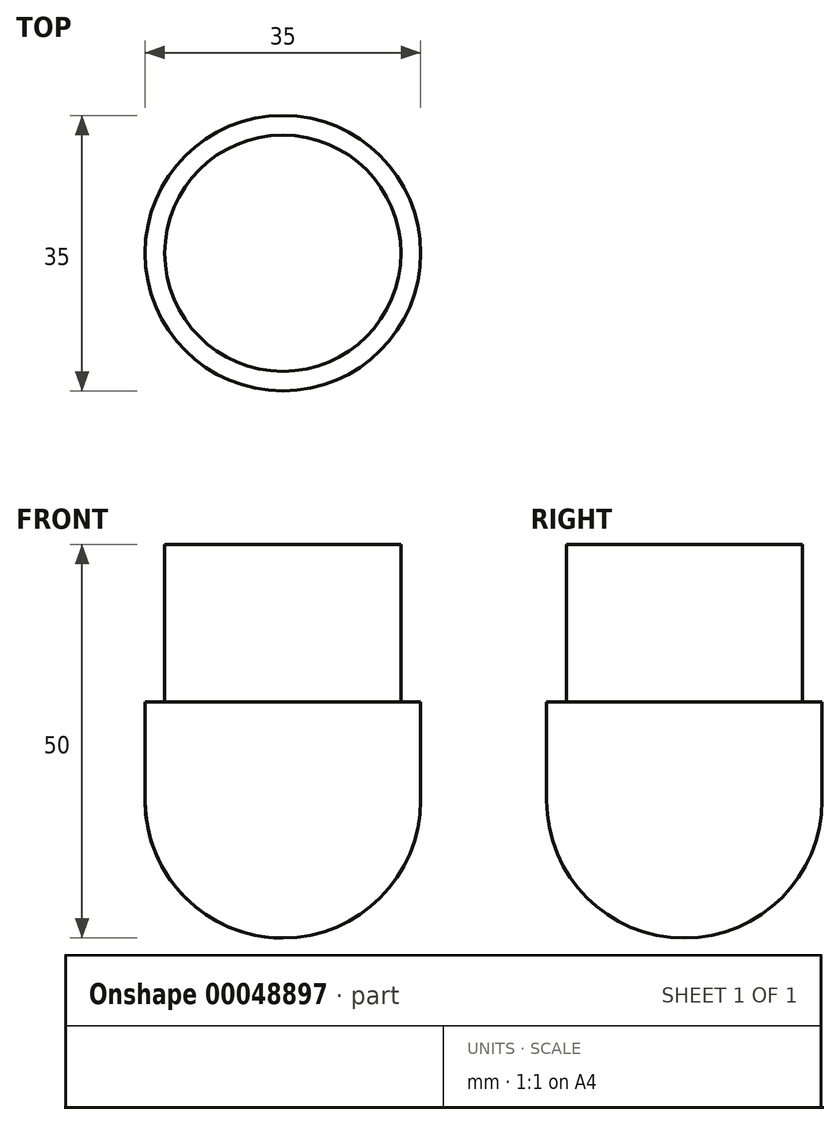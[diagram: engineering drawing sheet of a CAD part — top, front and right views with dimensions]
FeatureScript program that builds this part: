
annotation { "Feature Type Name" : "Feature", "Feature Type Description" : "" }
export const myFeature = defineFeature(function(context is Context, id is Id, definition is map)
    precondition{}
    {
        {
            var Q0;
            Q0=qCreatedBy(makeId("Top.planeOp"),FACE);
            var sketch = newSketch(context, id + "F0", { "sketchPlane" : qUnion([Q0])});
            skCircle(sketch, "E0", {"center": v(0, 0) * mm, "radius": 15 * mm});
            skSolve(sketch);
        }
        {
            var Q0;
            Q0=makeQuery(id+"F0.imprint","IMPRINT",FACE,{"disambiguationData":[TD([[makeQuery(id+"F0.imprint","IMPRINT",EDGE,{"derivedFrom":sQuery(id+"F0.wireOp",EDGE,"E0")}),1.0]])]});
            extrude(context, id + "F1", {"entities" : qUnion([Q0]), "depth" : 20 * mm});
        }
        {
            var Q0;
            Q0=makeQuery(id+"F1.opExtrude","CAP_FACE",FACE,{"disambiguationData":[OSD([sQuery(id+"F0.wireOp",EDGE,"E0")])],"isStart":true});
            var sketch = newSketch(context, id + "F2", { "sketchPlane" : qUnion([Q0])});
            skCircle(sketch, "E1", {"center": v(0, 0) * mm, "radius": 17.5 * mm});
            skSolve(sketch);
        }
        {
            var Q0;
            Q0=makeQuery(id+"F2.imprint","IMPRINT",FACE,{"disambiguationData":[TD([[makeQuery(id+"F2.imprint","IMPRINT",EDGE,{"derivedFrom":sQuery(id+"F2.wireOp",EDGE,"E1")}),1.0]])]});
            var Q1;
            Q1=makeQuery(id+"F2.imprint","IMPRINT",FACE,{"disambiguationData":[TD([[makeQuery(id+"F2.imprint","IMPRINT",EDGE,{"derivedFrom":makeQuery(id+"F1.opExtrude","CAP_EDGE",EDGE,{"disambiguationData":[OSD([sQuery(id+"F0.wireOp",EDGE,"E0")])],"isStart":true})}),-1.0]])]});
            extrude(context, id + "F3", {"entities" : qUnion([Q0, Q1]), "operationType" : NewBodyOperationType.ADD, "depth" : 30 * mm});
        }
        {
            var Q0;
            Q0=makeQuery(id+"F3.opExtrude","CAP_FACE",FACE,{"disambiguationData":[OSD([sQuery(id+"F2.wireOp",EDGE,"E1")])],"isStart":false});
            var sketch = newSketch(context, id + "F4", { "sketchPlane" : qUnion([Q0])});
            skLineSegment(sketch, "E2", {"start": v(0, 0) * mm, "end": v(0, 17.5) * mm, "construction": true});
            skLineSegment(sketch, "E3", {"start": v(0, 0) * mm, "end": v(0, -17.5) * mm, "construction": true});
            skLineSegment(sketch, "E4", {"start": v(0, 0) * mm, "end": v(-17.5, 0) * mm, "construction": true});
            skSolve(sketch);
        }
        {
            var Q0;
            Q0=makeQuery(id+"F3.opExtrude","CAP_EDGE",EDGE,{"disambiguationData":[OSD([sQuery(id+"F2.wireOp",EDGE,"E1")])],"isStart":false});
            fillet(context, id + "F5", {"entities" : qUnion([Q0]), "radius" : 17.5 * mm, "tangentPropagation" : true, "allowEdgeOverflow" : false});
        }
    });
